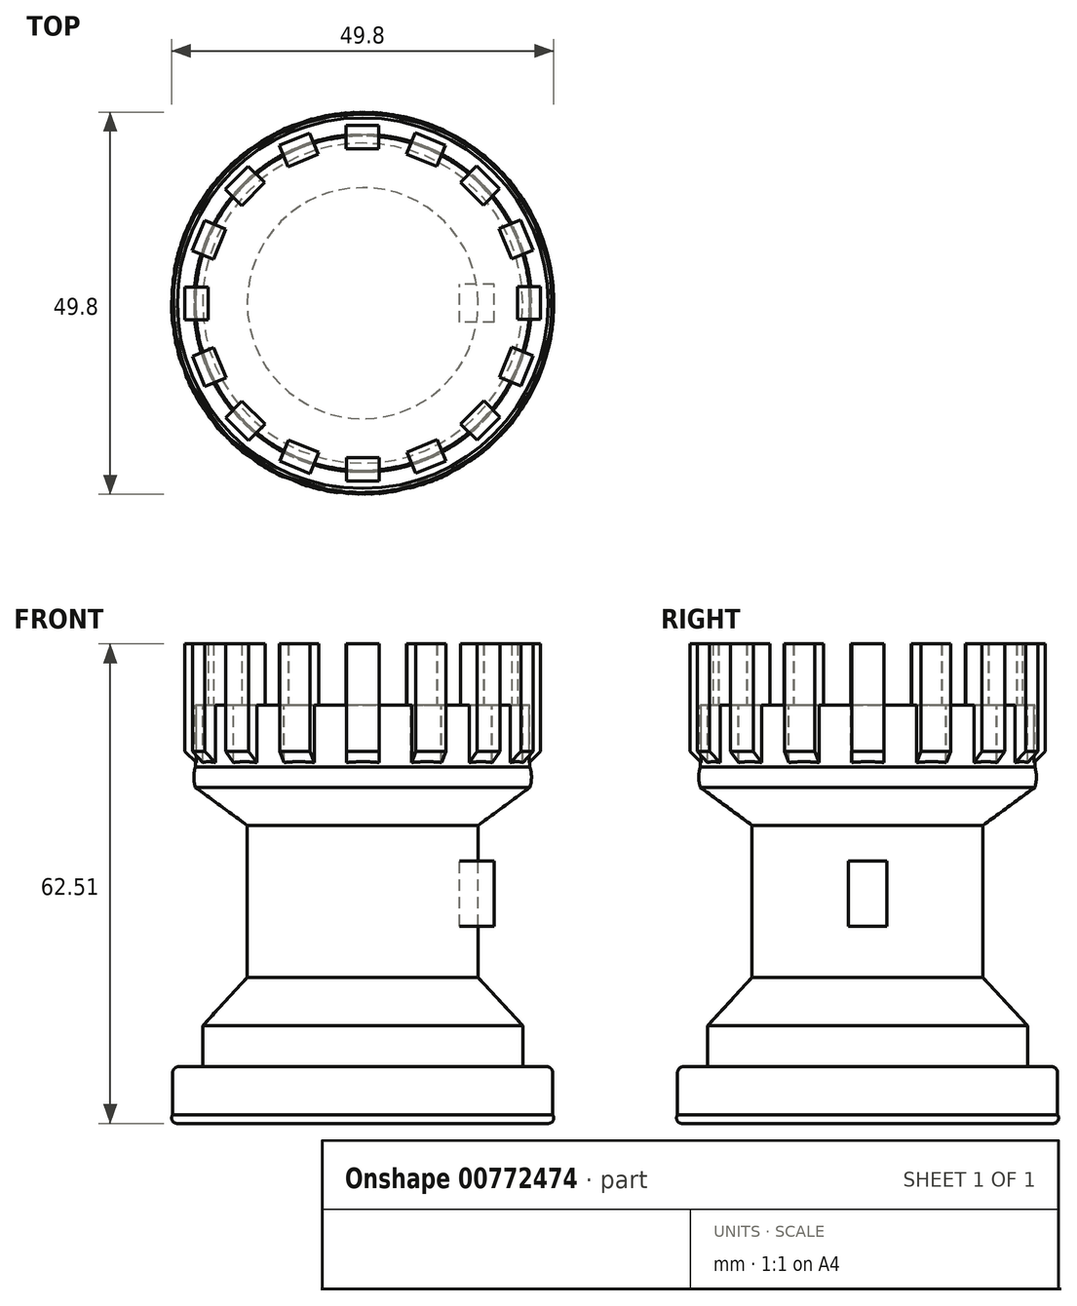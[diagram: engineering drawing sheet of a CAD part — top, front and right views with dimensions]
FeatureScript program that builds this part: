
annotation { "Feature Type Name" : "Feature", "Feature Type Description" : "" }
export const myFeature = defineFeature(function(context is Context, id is Id, definition is map)
    precondition{}
    {
        {
            var Q0;
            Q0=qCreatedBy(makeId("Front.planeOp"),FACE);
            var sketch = newSketch(context, id + "F0", { "sketchPlane" : qUnion([Q0])});
            skLineSegment(sketch, "E0", {"start": v(0, 0) * mm, "end": v(24.2, 0) * mm});
            skLineSegment(sketch, "E1", {"start": v(20.86, 12.72) * mm, "end": v(15.06, 19) * mm});
            skLineSegment(sketch, "E2", {"start": v(15.06, 19) * mm, "end": v(15.06, 38.86) * mm});
            skLineSegment(sketch, "E3", {"start": v(15.06, 38.86) * mm, "end": v(21.8, 43.8) * mm});
            skPoint(sketch, "E4.start.orphan", {"position": v(24.2, 6.92) * mm});
            skPoint(sketch, "E5.end.orphan", {"position": v(24.2, 7.73) * mm});
            skArc(sketch, "E6", {"start": v(24.2, 0) * mm, "mid": v(24.82, 0.38) * mm, "end": v(24.77, 1.1) * mm});
            skLineSegment(sketch, "E7", {"start": v(24.77, 1.1) * mm, "end": v(24.77, 6.59) * mm});
            skArc(sketch, "E8", {"start": v(24.77, 6.59) * mm, "mid": v(24.6, 7.09) * mm, "end": v(24.16, 7.38) * mm});
            skLineSegment(sketch, "E9", {"start": v(23.73, 7.38) * mm, "end": v(20.86, 7.38) * mm});
            skLineSegment(sketch, "E10", {"start": v(20.86, 12.72) * mm, "end": v(20.86, 7.38) * mm});
            skLineSegment(sketch, "E11", {"start": v(23.73, 7.38) * mm, "end": v(24.16, 7.38) * mm});
            skArc(sketch, "E12", {"start": v(21.8, 43.8) * mm, "mid": v(22, 45.14) * mm, "end": v(21.8, 46.48) * mm});
            skLineSegment(sketch, "E13", {"start": v(21.8, 46.48) * mm, "end": v(21.8, 54.5) * mm});
            skLineSegment(sketch, "E14", {"start": v(10.9, 54.5) * mm, "end": v(21.8, 54.5) * mm});
            skPoint(sketch, "E15.start.orphan", {"position": v(0, 55) * mm});
            skPoint(sketch, "E16.start.orphan", {"position": v(0, 54.5) * mm});
            skLineSegment(sketch, "E17.bottom", {"start": v(10.9, 54.5) * mm, "end": v(0, 54.5) * mm});
            skLineSegment(sketch, "E17.top", {"start": v(10.9, 0) * mm, "end": v(0, 0) * mm});
            skLineSegment(sketch, "E17.right", {"start": v(0, 54.5) * mm, "end": v(0, 0) * mm});
            skPoint(sketch, "E18.end.orphan", {"position": v(10.9, 0) * mm});
            skSolve(sketch);
        }
        {
            var Q0;
            Q0=makeQuery(id+"F0.imprint","IMPRINT",FACE,{"disambiguationData":[TD([[makeQuery(id+"F0.imprint","IMPRINT",EDGE,{"derivedFrom":sQuery(id+"F0.wireOp",EDGE,"E1")}),1.0]])]});
            var Q1;
            Q1=sQuery(id+"F0.wireOp",EDGE,"E17.right");
            revolve(context, id + "F1", {"surfaceOperationType" : NewSurfaceOperationType.NEW, "entities" : qUnion([Q0]), "axis" : qUnion([Q1]), "revolveType" : RevolveType.FULL});
        }
        {
            var Q0;
            Q0=makeQuery(id+"F1.opRevolve","SWEPT_FACE",FACE,{"disambiguationData":[OSD([sQuery(id+"F0.wireOp",EDGE,"E14"),sQuery(id+"F0.wireOp",EDGE,"E17.bottom")])]});
            var sketch = newSketch(context, id + "F2", { "sketchPlane" : qUnion([Q0])});
            skLineSegment(sketch, "E19.bottom", {"start": v(-2.08, -20.16) * mm, "end": v(2.16, -20.16) * mm});
            skLineSegment(sketch, "E19.top", {"start": v(-2.08, -23.16) * mm, "end": v(2.16, -23.16) * mm});
            skLineSegment(sketch, "E19.left", {"start": v(-2.08, -20.16) * mm, "end": v(-2.08, -23.16) * mm});
            skLineSegment(sketch, "E19.right", {"start": v(2.16, -20.16) * mm, "end": v(2.16, -23.16) * mm});
            skSolve(sketch);
        }
        {
            var Q0;
            {var subQ0=sQuery(id+"F2.wireOp",EDGE,"E19.top");Q0=makeQuery(id+"F2.imprint","IMPRINT",FACE,{"disambiguationData":[TD([[makeQuery(id+"F2.imprint","IMPRINT",EDGE,{"derivedFrom":subQ0}),1.0]])]});}
            var Q1;
            {var subQ0=sQuery(id+"F2.wireOp",EDGE,"E19.bottom");Q1=makeQuery(id+"F2.imprint","IMPRINT",FACE,{"disambiguationData":[TD([[makeQuery(id+"F2.imprint","IMPRINT",EDGE,{"derivedFrom":subQ0}),-1.0]])]});}
            extrude(context, id + "F3", {"entities" : qUnion([Q0, Q1]), "operationType" : NewBodyOperationType.ADD, "endBound" : BoundingType.SYMMETRIC, "depth" : 16 * mm, "offsetDistance" : 25 * mm});
        }
        {
            var Q0;
            Q0=makeQuery(id+"F3.opExtrude","CAP_EDGE",EDGE,{"disambiguationData":[OSD([sQuery(id+"F2.wireOp",EDGE,"E19.top")])],"isStart":true});
            chamfer(context, id + "F4", {"entities" : qUnion([Q0]), "chamferType" : ChamferType.OFFSET_ANGLE, "width" : 2 * mm, "oppositeDirection" : false, "angle" : 45 * degree, "tangentPropagation" : true});
        }
        {
            var Q0;
            Q0=makeQuery(id+"F1.opRevolve","SWEPT_BODY",BODY,{"disambiguationData":[OSD([sQuery(id+"F0.wireOp",EDGE,"E0"),sQuery(id+"F0.wireOp",EDGE,"E1"),sQuery(id+"F0.wireOp",EDGE,"E2"),sQuery(id+"F0.wireOp",EDGE,"E3"),sQuery(id+"F0.wireOp",EDGE,"E6"),sQuery(id+"F0.wireOp",EDGE,"E7"),sQuery(id+"F0.wireOp",EDGE,"E8"),sQuery(id+"F0.wireOp",EDGE,"E9"),sQuery(id+"F0.wireOp",EDGE,"E10"),sQuery(id+"F0.wireOp",EDGE,"E11"),sQuery(id+"F0.wireOp",EDGE,"E12"),sQuery(id+"F0.wireOp",EDGE,"E13"),sQuery(id+"F0.wireOp",EDGE,"E14"),sQuery(id+"F0.wireOp",EDGE,"E17.bottom"),sQuery(id+"F0.wireOp",EDGE,"E17.right")])]});
            var Q1;
            Q1=makeQuery(id+"F1.opRevolve","SWEPT_FACE",FACE,{"disambiguationData":[OSD([sQuery(id+"F0.wireOp",EDGE,"E13")])]});
            circularPattern(context, id + "F5", {"entities" : qUnion([Q0]), "axis" : qUnion([Q1]), "angle" : 360 * degree, "instanceCount" : 16, "equalSpace" : true});
        }
        {
            var Q0;
            Q0=qCreatedBy(makeId("Front.planeOp"),FACE);
            var sketch = newSketch(context, id + "F6", { "sketchPlane" : qUnion([Q0])});
            skLineSegment(sketch, "E20.bottom", {"start": v(17.15, 25.71) * mm, "end": v(12.63, 25.71) * mm});
            skLineSegment(sketch, "E20.top", {"start": v(17.15, 34.21) * mm, "end": v(12.63, 34.21) * mm});
            skLineSegment(sketch, "E20.left", {"start": v(17.15, 25.71) * mm, "end": v(17.15, 34.21) * mm});
            skLineSegment(sketch, "E20.right", {"start": v(12.63, 25.71) * mm, "end": v(12.63, 34.21) * mm});
            skPoint(sketch, "E20.middle", {"position": v(14.9, 29.96) * mm});
            skSolve(sketch);
        }
        {
            var Q0;
            Q0=makeQuery(id+"F6.imprint","IMPRINT",FACE,{"disambiguationData":[TD([[makeQuery(id+"F6.imprint","IMPRINT",EDGE,{"derivedFrom":sQuery(id+"F6.wireOp",EDGE,"E20.bottom")}),-1.0]])]});
            extrude(context, id + "F7", {"entities" : qUnion([Q0]), "endBound" : BoundingType.SYMMETRIC, "depth" : 5 * mm, "offsetDistance" : 25 * mm});
        }
    });
